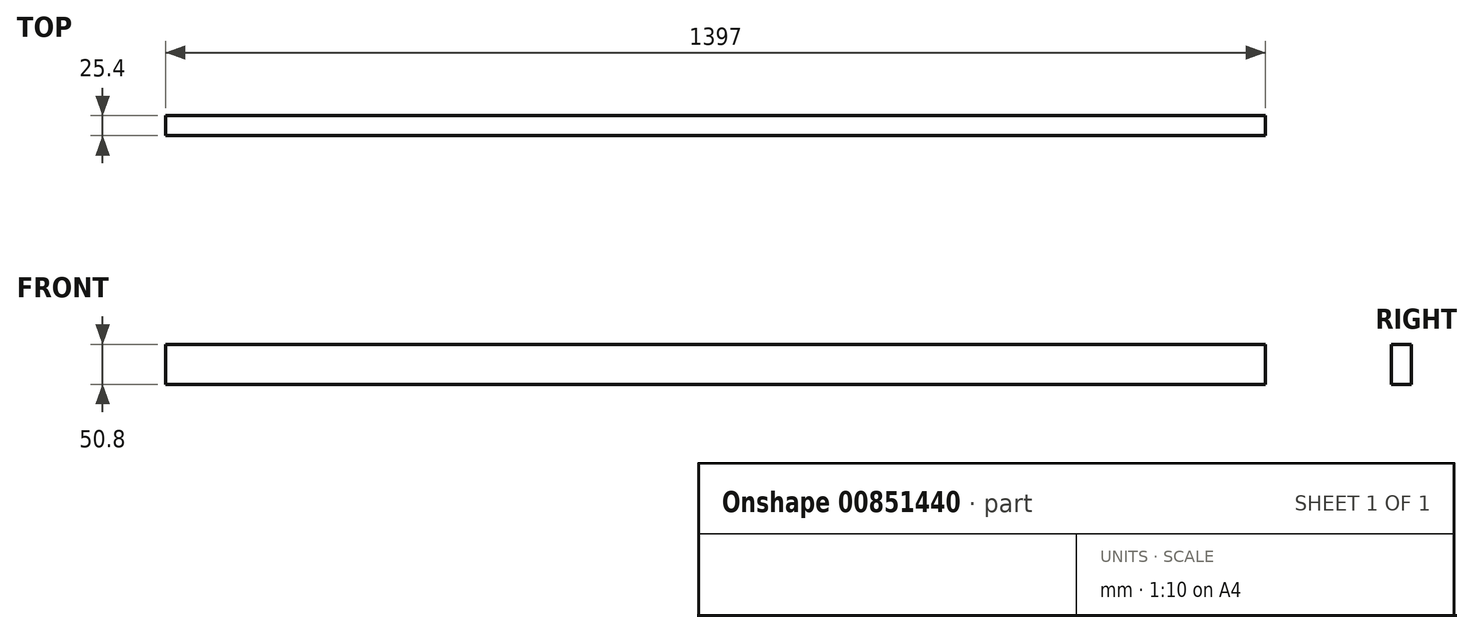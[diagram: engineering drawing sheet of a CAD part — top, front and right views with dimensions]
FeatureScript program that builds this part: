
annotation { "Feature Type Name" : "Feature", "Feature Type Description" : "" }
export const myFeature = defineFeature(function(context is Context, id is Id, definition is map)
    precondition{}
    {
        {
            var Q0;
            Q0=qCreatedBy(makeId("Front.planeOp"),FACE);
            var sketch = newSketch(context, id + "F0", { "sketchPlane" : qUnion([Q0])});
            skLineSegment(sketch, "E0", {"start": v(0, 0) * mm, "end": v(1397, 0) * mm});
            skLineSegment(sketch, "E1", {"start": v(1397, 0) * mm, "end": v(1397, 50.8) * mm});
            skLineSegment(sketch, "E2", {"start": v(1397, 50.8) * mm, "end": v(0, 50.8) * mm});
            skLineSegment(sketch, "E3", {"start": v(0, 50.8) * mm, "end": v(0, 0) * mm});
            skSolve(sketch);
        }
        {
            var Q0;
            Q0 = qSketchRegion(id + "F0", true);
            extrude(context, id + "F1", {"entities" : qUnion([Q0]), "depth" : 25.4 * mm, "offsetDistance" : 25.4 * mm});
        }
    });
